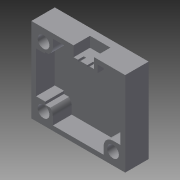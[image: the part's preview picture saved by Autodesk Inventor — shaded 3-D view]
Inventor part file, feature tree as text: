
AUTODESK INVENTOR PART (.ipt)
format: ipt  version: 2015 SP1 (Build 190203100, 203)  size: 242,688 bytes
history: native  units: mm
features: extrude x5, sketch x3, other x1, projected_geometry x1
ambient origin geometry x8: Origin, YZ Plane, XZ Plane, XY Plane, X Axis, Y Axis, Z Axis, Center Point
bodies: Body1 (feature_tree)
feature tree (10):
  other  "Твердое тело1"
  sketch  "Эскиз1"
  extrude  "Выдавливание1"  Depth=36.0mm
  extrude  "Выдавливание2"  Depth=32.0mm
  extrude  "Выдавливание3"  Depth=3.18mm
  extrude  "Выдавливание4"  Depth=3.18mm
  extrude  "Выдавливание5"  Depth=3.18mm
  sketch  "Эскиз2"
  sketch  "Эскиз4"
  projected_geometry  "Спроецированная петля1"
